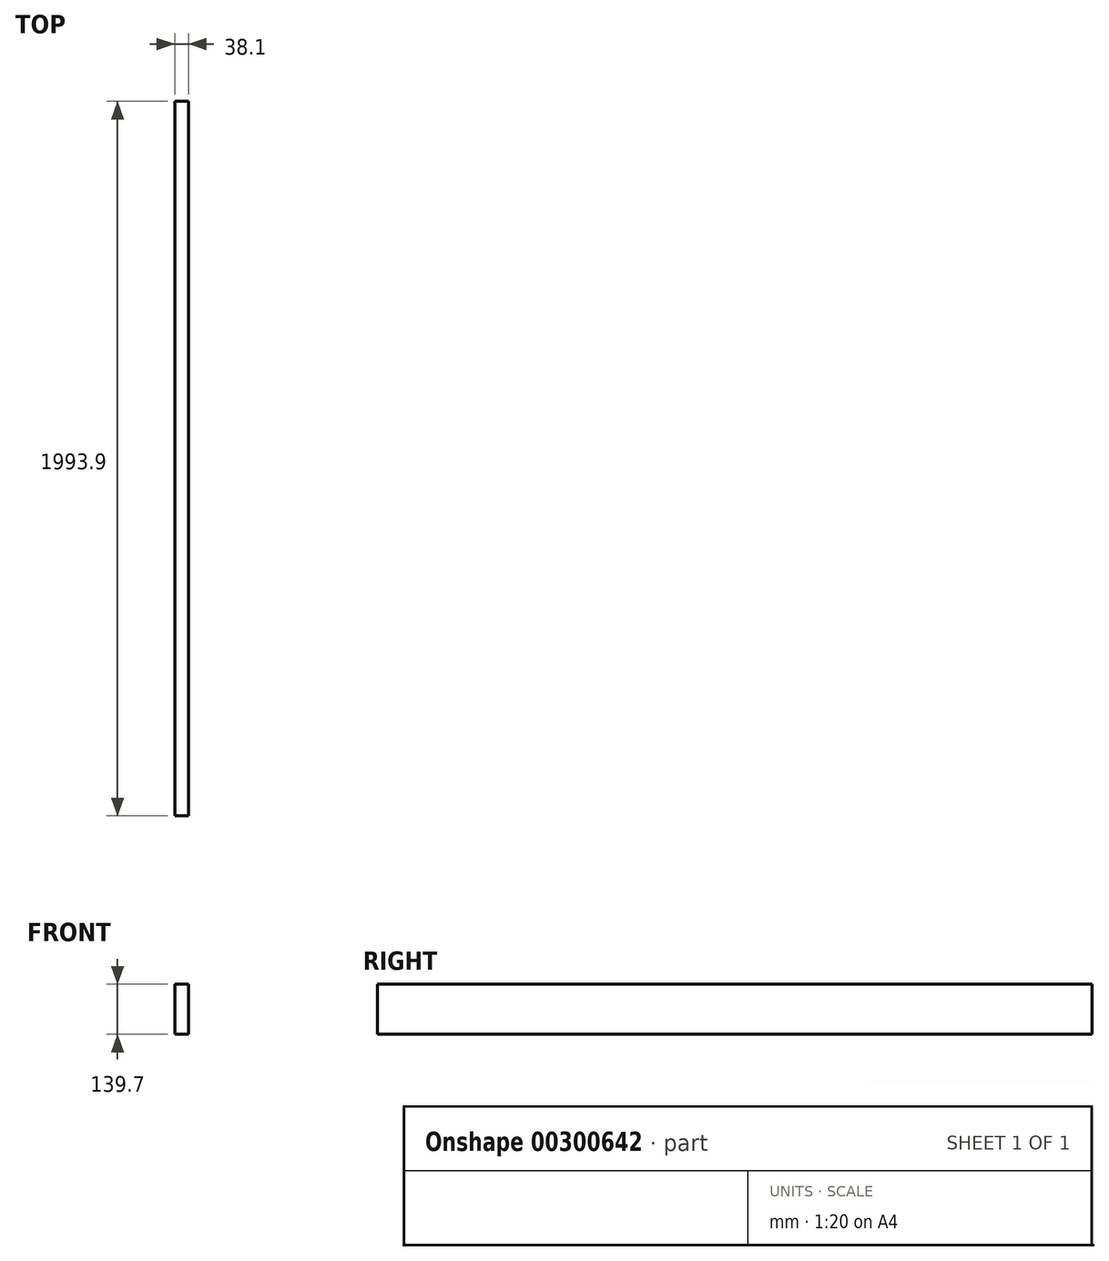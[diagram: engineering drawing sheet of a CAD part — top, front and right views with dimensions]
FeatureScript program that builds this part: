
annotation { "Feature Type Name" : "Feature", "Feature Type Description" : "" }
export const myFeature = defineFeature(function(context is Context, id is Id, definition is map)
    precondition{}
    {
        {
            var Q0;
            Q0=qCreatedBy(makeId("Front.planeOp"),FACE);
            var sketch = newSketch(context, id + "F0", { "sketchPlane" : qUnion([Q0])});
            skLineSegment(sketch, "E0.bottom", {"start": v(19.05, 69.85) * mm, "end": v(-19.05, 69.85) * mm});
            skLineSegment(sketch, "E0.top", {"start": v(19.05, -69.85) * mm, "end": v(-19.05, -69.85) * mm});
            skLineSegment(sketch, "E0.left", {"start": v(19.05, 69.85) * mm, "end": v(19.05, -69.85) * mm});
            skLineSegment(sketch, "E0.right", {"start": v(-19.05, 69.85) * mm, "end": v(-19.05, -69.85) * mm});
            skPoint(sketch, "E0.middle", {"position": v(0, 0) * mm});
            skSolve(sketch);
        }
        {
            var Q0;
            Q0=qSketchRegion(id+"F0",true);
            extrude(context, id + "F1", {"entities" : qUnion([Q0]), "oppositeDirection" : true, "depth" : 1993.9 * mm});
        }
    });
